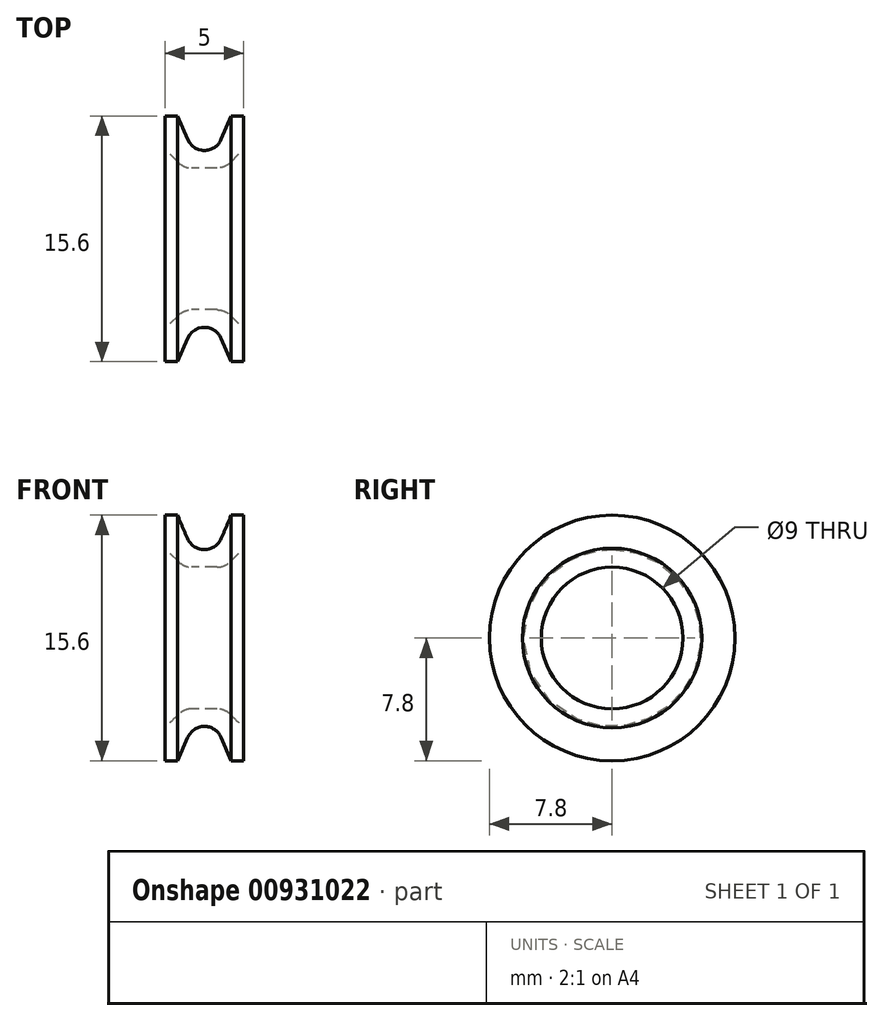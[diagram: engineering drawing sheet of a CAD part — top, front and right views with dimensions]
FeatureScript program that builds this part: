
annotation { "Feature Type Name" : "Feature", "Feature Type Description" : "" }
export const myFeature = defineFeature(function(context is Context, id is Id, definition is map)
    precondition{}
    {
        {
            assignVariable(context, id + "F0", {"name" : "width", "anyValue" : 5});
        }
        {
            var Q0;
            Q0=qCreatedBy(makeId("Right.planeOp"),FACE);
            var sketch = newSketch(context, id + "F1", { "sketchPlane" : qUnion([Q0])});
            skCircle(sketch, "E0", {"center": v(0, 0) * mm, "radius": 5 * mm});
            skCircle(sketch, "E1", {"center": v(0, 0) * mm, "radius": 4.5 * mm});
            skSolve(sketch);
        }
        {
            var Q0;
            Q0=qCreatedBy(makeId("Front.planeOp"),FACE);
            var sketch = newSketch(context, id + "F2", { "sketchPlane" : qUnion([Q0])});
            skLineSegment(sketch, "E2", {"start": v(-2.5, 5) * mm, "end": v(2.5, 5) * mm});
            skLineSegment(sketch, "E3.0", {"start": v(0, 5) * mm, "end": v(0, -5) * mm});
            skLineSegment(sketch, "E4", {"start": v(-2.5, 5) * mm, "end": v(-2.5, 7.8) * mm});
            skLineSegment(sketch, "E5", {"start": v(2.5, 5) * mm, "end": v(2.5, 7.8) * mm});
            skLineSegment(sketch, "E6", {"start": v(-2.5, 7.8) * mm, "end": v(-1.7, 7.8) * mm});
            skLineSegment(sketch, "E7", {"start": v(2.5, 7.8) * mm, "end": v(1.7, 7.8) * mm});
            skLineSegment(sketch, "E8", {"start": v(1.7, 7.8) * mm, "end": v(1.07, 6.33) * mm});
            skLineSegment(sketch, "E9", {"start": v(-1.7, 7.8) * mm, "end": v(-1.07, 6.33) * mm});
            skArc(sketch, "E10", {"start": v(-1.07, 6.33) * mm, "mid": v(0, 5.62) * mm, "end": v(1.07, 6.33) * mm});
            skSolve(sketch);
        }
        {
            var Q0;
            Q0=makeQuery(id+"F1.imprint","IMPRINT",FACE,{"disambiguationData":[TD([[makeQuery(id+"F1.imprint","IMPRINT",EDGE,{"derivedFrom":sQuery(id+"F1.wireOp",EDGE,"E0")}),1.0]])]});
            extrude(context, id + "F3", {"entities" : qUnion([Q0]), "endBound" : BoundingType.SYMMETRIC, "depth" : (getVariable(context, 'width')) * mm, "offsetDistance" : 25 * mm});
        }
        {
            var Q0;
            {var subQ1=sQuery(id+"F2.wireOp",EDGE,"E4");Q0=makeQuery(id+"F2.imprint","IMPRINT",FACE,{"disambiguationData":[TD([[makeQuery(id+"F2.imprint","IMPRINT",EDGE,{"derivedFrom":subQ1}),-1.0]])]});}
            var Q1;
            {var subQ0=sQuery(id+"F2.wireOp",EDGE,"E5");Q1=makeQuery(id+"F2.imprint","IMPRINT",FACE,{"disambiguationData":[TD([[makeQuery(id+"F2.imprint","IMPRINT",EDGE,{"derivedFrom":subQ0}),1.0]])]});}
            var Q2;
            Q2=sQuery(id+"F1.wireOp",EDGE,"E0");
            revolve(context, id + "F4", {"operationType" : NewBodyOperationType.ADD, "surfaceOperationType" : NewSurfaceOperationType.NEW, "entities" : qUnion([Q0, Q1]), "axis" : qUnion([Q2]), "revolveType" : RevolveType.FULL});
        }
        {
            var Q0;
            Q0=makeQuery(id+"F3.opExtrude","CAP_EDGE",EDGE,{"disambiguationData":[OSD([sQuery(id+"F1.wireOp",EDGE,"E1")])],"isStart":true});
            var Q1;
            Q1=makeQuery(id+"F3.opExtrude","CAP_EDGE",EDGE,{"disambiguationData":[OSD([sQuery(id+"F1.wireOp",EDGE,"E1")])],"isStart":false});
            chamfer(context, id + "F5", {"entities" : qUnion([Q0, Q1]), "width" : 1.2 * mm, "tangentPropagation" : true});
        }
        {
            var Q0;
            {var subQ0=sQuery(id+"F1.wireOp",EDGE,"E0");var subQ1=makeQuery(id+"FB64yhed25rAMYw_1.opExtrude","SWEPT_FACE",FACE,{"disambiguationData":[OSD([subQ0])]});Q0=makeQuery(id+"F5.opChamfer","BLEND_EDGE",EDGE,{"blendedFrom":[makeQuery(id+"FB64yhed25rAMYw_1.boolean.opBoolean","INTERSECT",EDGE,{"derivedFrom":[makeQuery(id+"F4.boolean.opBoolean","MERGE",FACE,{"derivedFrom":[makeQuery(id+"F3.opExtrude","CAP_FACE",FACE,{"disambiguationData":[OSD([subQ0])],"isStart":true}),makeQuery(id+"F4.opRevolve","SWEPT_FACE",FACE,{"disambiguationData":[OSD([sQuery(id+"F2.wireOp",EDGE,"E4")])]})]}),subQ1]}),makeQuery(id+"FB64yhed25rAMYw_1.boolean.opBoolean","COPY",FACE,{"derivedFrom":subQ1})],"blendedInto":[makeQuery(id+"FB64yhed25rAMYw_1.boolean.opBoolean","COPY",FACE,{"derivedFrom":subQ1})]});}
            var Q1;
            {var subQ0=sQuery(id+"F1.wireOp",EDGE,"E0");var subQ1=makeQuery(id+"FB64yhed25rAMYw_1.opExtrude","SWEPT_FACE",FACE,{"disambiguationData":[OSD([subQ0])]});Q1=makeQuery(id+"F5.opChamfer","BLEND_EDGE",EDGE,{"blendedFrom":[makeQuery(id+"FB64yhed25rAMYw_1.boolean.opBoolean","INTERSECT",EDGE,{"derivedFrom":[makeQuery(id+"F4.boolean.opBoolean","MERGE",FACE,{"derivedFrom":[makeQuery(id+"F3.opExtrude","CAP_FACE",FACE,{"disambiguationData":[OSD([subQ0])],"isStart":false}),makeQuery(id+"F4.opRevolve","SWEPT_FACE",FACE,{"disambiguationData":[OSD([sQuery(id+"F2.wireOp",EDGE,"E5")])]})]}),subQ1]}),makeQuery(id+"FB64yhed25rAMYw_1.boolean.opBoolean","COPY",FACE,{"derivedFrom":subQ1})],"blendedInto":[makeQuery(id+"FB64yhed25rAMYw_1.boolean.opBoolean","COPY",FACE,{"derivedFrom":subQ1})]});}
            var Q2;
            {var subQ0=sQuery(id+"F1.wireOp",EDGE,"E1");Q2=makeQuery(id+"F5.opChamfer","BLEND_EDGE",EDGE,{"blendedFrom":[makeQuery(id+"F3.opExtrude","CAP_EDGE",EDGE,{"disambiguationData":[OSD([subQ0])],"isStart":false}),makeQuery(id+"F3.opExtrude","SWEPT_FACE",FACE,{"disambiguationData":[OSD([subQ0])]})],"blendedInto":[makeQuery(id+"F3.opExtrude","SWEPT_FACE",FACE,{"disambiguationData":[OSD([subQ0])]})]});}
            var Q3;
            {var subQ0=sQuery(id+"F1.wireOp",EDGE,"E1");Q3=makeQuery(id+"F5.opChamfer","BLEND_EDGE",EDGE,{"blendedFrom":[makeQuery(id+"F3.opExtrude","CAP_EDGE",EDGE,{"disambiguationData":[OSD([subQ0])],"isStart":true}),makeQuery(id+"F3.opExtrude","SWEPT_FACE",FACE,{"disambiguationData":[OSD([subQ0])]})],"blendedInto":[makeQuery(id+"F3.opExtrude","SWEPT_FACE",FACE,{"disambiguationData":[OSD([subQ0])]})]});}
            fillet(context, id + "F6", {"entities" : qUnion([Q0, Q1, Q2, Q3]), "radius" : 1.2 * mm, "tangentPropagation" : true, "allowEdgeOverflow" : false});
        }
    });
